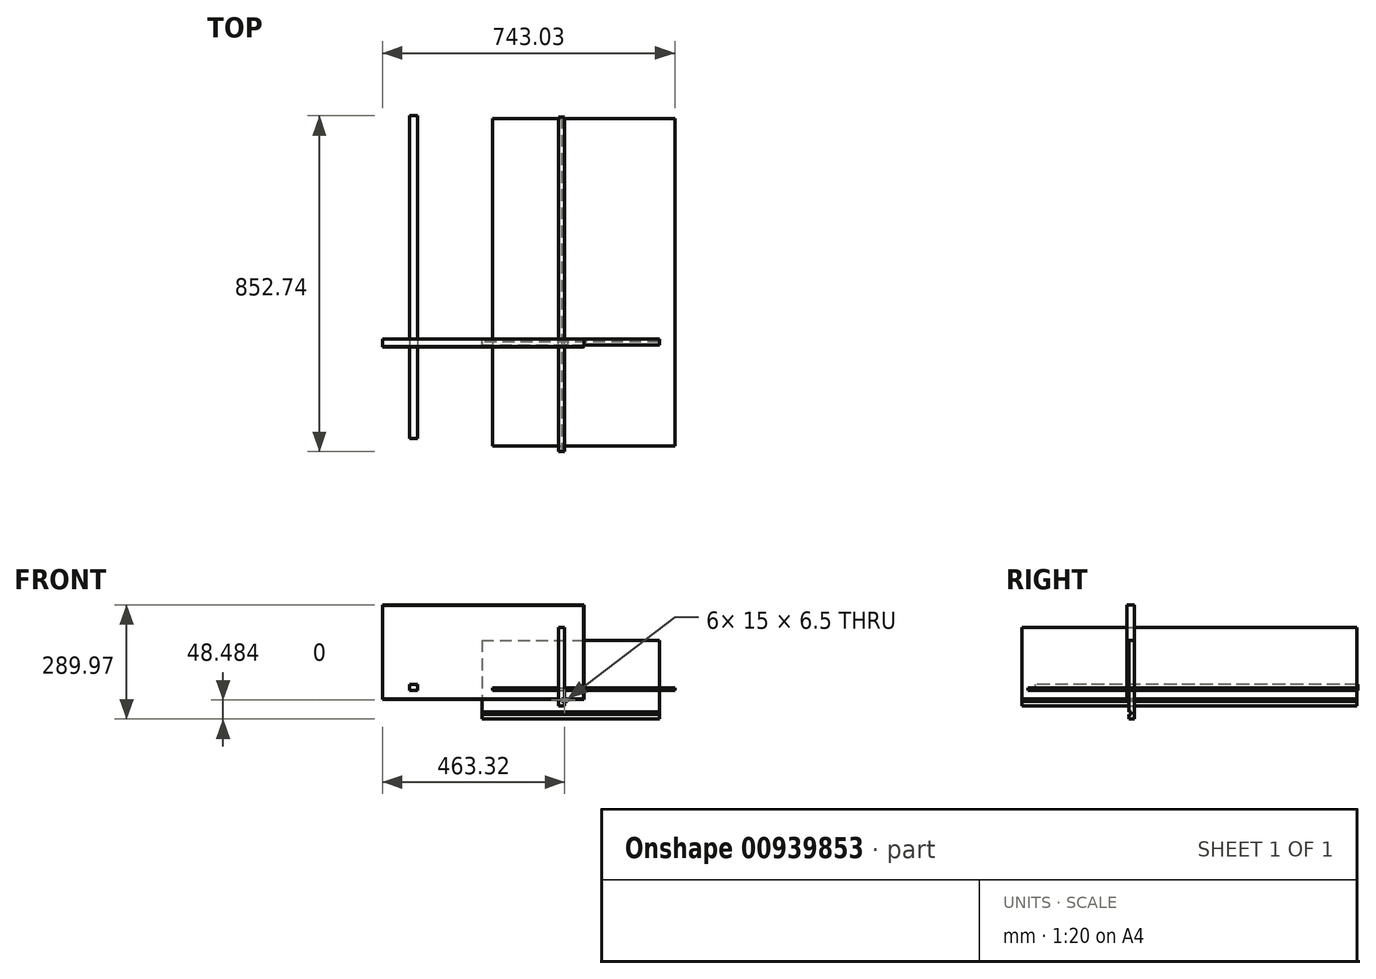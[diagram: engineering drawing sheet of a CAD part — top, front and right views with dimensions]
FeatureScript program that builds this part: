
annotation { "Feature Type Name" : "Feature", "Feature Type Description" : "" }
export const myFeature = defineFeature(function(context is Context, id is Id, definition is map)
    precondition{}
    {
        {
            var Q0;
            Q0=qCreatedBy(makeId("Front.planeOp"),FACE);
            var sketch = newSketch(context, id + "F0", { "sketchPlane" : qUnion([Q0])});
            skLineSegment(sketch, "E0.bottom", {"start": v(-447.82, 216.68) * mm, "end": v(64.18, 216.68) * mm});
            skLineSegment(sketch, "E0.top", {"start": v(-447.82, -23.32) * mm, "end": v(64.18, -23.32) * mm});
            skLineSegment(sketch, "E0.left", {"start": v(-447.82, 216.68) * mm, "end": v(-447.82, -23.32) * mm});
            skLineSegment(sketch, "E0.right", {"start": v(64.18, 216.68) * mm, "end": v(64.18, -23.32) * mm});
            skSolve(sketch);
        }
        {
            var Q0;
            Q0=qSketchRegion(id+"F0",true);
            extrude(context, id + "F1", {"entities" : qUnion([Q0]), "depth" : 20 * mm, "offsetDistance" : 25 * mm});
        }
        {
            var Q0;
            Q0=makeQuery(id+"F1.opExtrude","CAP_EDGE",EDGE,{"disambiguationData":[OSD([sQuery(id+"F0.wireOp",EDGE,"E0.top")])],"isStart":false});
            var Q1;
            Q1=makeQuery(id+"F1.opExtrude","CAP_FACE",FACE,{"disambiguationData":[OSD([sQuery(id+"F0.wireOp",EDGE,"E0.bottom"),sQuery(id+"F0.wireOp",EDGE,"E0.top"),sQuery(id+"F0.wireOp",EDGE,"E0.left"),sQuery(id+"F0.wireOp",EDGE,"E0.right")])],"isStart":false});
            chamfer(context, id + "F2", {"entities" : qUnion([Q0, Q1]), "width" : 1 * mm, "tangentPropagation" : true});
        }
        {
            var Q0;
            Q0=qCreatedBy(makeId("Right.planeOp"),FACE);
            var sketch = newSketch(context, id + "F3", { "sketchPlane" : qUnion([Q0])});
            skLineSegment(sketch, "E1.bottom", {"start": v(-285.75, 159.94) * mm, "end": v(564.25, 159.94) * mm});
            skLineSegment(sketch, "E1.top", {"start": v(-285.75, -40.06) * mm, "end": v(564.25, -40.06) * mm});
            skLineSegment(sketch, "E1.left", {"start": v(-285.75, 159.94) * mm, "end": v(-285.75, -40.06) * mm});
            skLineSegment(sketch, "E1.right", {"start": v(564.25, 159.94) * mm, "end": v(564.25, -40.06) * mm});
            skSolve(sketch);
        }
        {
            var Q0;
            Q0=qSketchRegion(id+"F3",true);
            extrude(context, id + "F4", {"entities" : qUnion([Q0]), "depth" : 15 * mm, "offsetDistance" : 25 * mm});
        }
        {
            var Q0;
            Q0=makeQuery(id+"F4.opExtrude","SWEPT_FACE",FACE,{"disambiguationData":[OSD([sQuery(id+"F3.wireOp",EDGE,"E1.left")])]});
            var sketch = newSketch(context, id + "F5", { "sketchPlane" : qUnion([Q0])});
            skLineSegment(sketch, "E2.bottom", {"start": v(23, -21.56) * mm, "end": v(8, -21.56) * mm});
            skLineSegment(sketch, "E2.top", {"start": v(23, -28.06) * mm, "end": v(8, -28.06) * mm});
            skLineSegment(sketch, "E2.left", {"start": v(23, -21.56) * mm, "end": v(23, -28.06) * mm});
            skLineSegment(sketch, "E2.right", {"start": v(8, -21.56) * mm, "end": v(8, -28.06) * mm});
            skSolve(sketch);
        }
        {
            var Q0;
            Q0=qSketchRegion(id+"F5",true);
            extrude(context, id + "F6", {"entities" : qUnion([Q0]), "operationType" : NewBodyOperationType.REMOVE, "oppositeDirection" : true, "depth" : 1000 * mm, "offsetDistance" : 25 * mm});
        }
        {
            var Q0;
            Q0=qCreatedBy(makeId("Front.planeOp"),FACE);
            var sketch = newSketch(context, id + "F7", { "sketchPlane" : qUnion([Q0])});
            skLineSegment(sketch, "E3.bottom", {"start": v(-195.11, 126.71) * mm, "end": v(255.89, 126.71) * mm});
            skLineSegment(sketch, "E3.top", {"start": v(-195.11, -73.29) * mm, "end": v(255.89, -73.29) * mm});
            skLineSegment(sketch, "E3.left", {"start": v(-195.11, 126.71) * mm, "end": v(-195.11, -73.29) * mm});
            skLineSegment(sketch, "E3.right", {"start": v(255.89, 126.71) * mm, "end": v(255.89, -73.29) * mm});
            skSolve(sketch);
        }
        {
            var Q0;
            Q0 = qSketchRegion(id + "F7", true);
            extrude(context, id + "F8", {"entities" : qUnion([Q0]), "depth" : 15 * mm, "offsetDistance" : 25 * mm});
        }
        {
            var Q0;
            Q0=makeQuery(id+"F8.opExtrude","SWEPT_FACE",FACE,{"disambiguationData":[OSD([sQuery(id+"F7.wireOp",EDGE,"E3.left")])]});
            var sketch = newSketch(context, id + "F9", { "sketchPlane" : qUnion([Q0])});
            skLineSegment(sketch, "E4.bottom", {"start": v(8, -54.79) * mm, "end": v(25.3, -54.79) * mm});
            skLineSegment(sketch, "E4.top", {"start": v(8, -61.29) * mm, "end": v(25.3, -61.29) * mm});
            skLineSegment(sketch, "E4.left", {"start": v(8, -54.79) * mm, "end": v(8, -61.29) * mm});
            skLineSegment(sketch, "E4.right", {"start": v(25.3, -54.79) * mm, "end": v(25.3, -61.29) * mm});
            skSolve(sketch);
        }
        {
            var Q0;
            Q0 = qSketchRegion(id + "F9", true);
            extrude(context, id + "F10", {"entities" : qUnion([Q0]), "operationType" : NewBodyOperationType.REMOVE, "oppositeDirection" : true, "depth" : 1000 * mm, "offsetDistance" : 25 * mm});
        }
        {
            var Q0;
            Q0=qCreatedBy(makeId("Top.planeOp"),FACE);
            var sketch = newSketch(context, id + "F11", { "sketchPlane" : qUnion([Q0])});
            skLineSegment(sketch, "E5.bottom", {"start": v(-167.79, 560.48) * mm, "end": v(295.21, 560.48) * mm});
            skLineSegment(sketch, "E5.top", {"start": v(-167.79, -271.52) * mm, "end": v(295.21, -271.52) * mm});
            skLineSegment(sketch, "E5.left", {"start": v(-167.79, 560.48) * mm, "end": v(-167.79, -271.52) * mm});
            skLineSegment(sketch, "E5.right", {"start": v(295.21, 560.48) * mm, "end": v(295.21, -271.52) * mm});
            skSolve(sketch);
        }
        {
            var Q0;
            Q0 = qSketchRegion(id + "F11", true);
            extrude(context, id + "F12", {"entities" : qUnion([Q0]), "depth" : 6.5 * mm, "offsetDistance" : 25 * mm});
        }
        {
            var Q0;
            Q0=qCreatedBy(makeId("Top.planeOp"),FACE);
            var sketch = newSketch(context, id + "F13", { "sketchPlane" : qUnion([Q0])});
            skLineSegment(sketch, "E6.bottom", {"start": v(-378.22, 566.99) * mm, "end": v(-358.22, 566.99) * mm});
            skLineSegment(sketch, "E6.top", {"start": v(-378.22, -253.01) * mm, "end": v(-358.22, -253.01) * mm});
            skLineSegment(sketch, "E6.left", {"start": v(-378.22, 566.99) * mm, "end": v(-378.22, -253.01) * mm});
            skLineSegment(sketch, "E6.right", {"start": v(-358.22, 566.99) * mm, "end": v(-358.22, -253.01) * mm});
            skSolve(sketch);
        }
        {
            var Q0;
            Q0 = qSketchRegion(id + "F13", true);
            extrude(context, id + "F14", {"entities" : qUnion([Q0]), "depth" : 15 * mm, "offsetDistance" : 25 * mm});
        }
    });
